# Revit family: Water_Heaters_HAJDU_HAJDU-HPT-200-and-200C_
name_source: partatom
category: Mechanical Equipment
units: mm (PartAtom-declared; Revit-internal decimal feet)

## family parameters
Always vertical = Yes
Classification = None
Cut with Voids When Loaded = No
Maintain Annotation Orientation = No
OmniClass Number = 23.31.29.13
OmniClass Title = Hot Water Tank Heaters
Part Type = Normal
Room Calculation Point = No
Round Connector Dimension = Use Diameter
Shared = No
Work Plane-Based = Yes

## types (2) — shared parameters
COP 20 °C = 3.36
COP 7 °C = 2.92
Case Material = Hajdu - Felület - Fehér
Cirkuláció bemenet = 19.05 mm  [stored 0.0625 ft]
Csapolási profil = L
Csatlakozás leírása = Elektromos csatlakozó
Default Elevation = 1219.2 mm  [stored 4 ft]
Description = A HB készülékek mellett, a HAJDU hőszivattyús forróvíztárolók másik termékcsaládja a HPT-k. Kisebb teljesítmény felvétel jellemzi max. hőszivattyús üzemmódban, illetve vízmelegítési hatékonysága is magasabb.A hőszivattyúból kiáramló levegővel hűthetjük a belső helyiségeket, vagy ha a lehűtött levegőt kivezetjük, akkor a helyiség vagy lakás szellőzését is szolgálhatja. A készülék a ház szellőztető rendszeréhez is csatlakoztatható. A használati melegvíz előállítás mellett így, ezek a készülékek a szellőztetésben, légkondicionálásban és páramentesítésben is szerepet kaphatnak.  Az elektromos fűtőtest segítségével a használati víz 65 °C-ra felmelegíthető.
Elektromos bekötés = fix
Energiahatékonysági osztály = A+
Feszültség = 230 V
Frekvencia = 50 Hz
Fázisok száma = 1
Hoszigetelés/vastagság = freonmentes PUR szigetelés / 50 mm
Hutoközeg/mennyiség = 1300g/R134a
Kompresszor teljesítmény felvétel max. = 900 W
Kompresszor teljesítmény felvétel átlagos = 515 W
Kondenzátor = biztonsági hőcserélő
Korrózióvédelem = speciális tűzzománc + Mg aktív anód
Látszólagos terhelés = 3680 VA
Légcsatorna csatlakozás = 160 mm  [stored 0.524934 ft]
Légáramlás = 125.0 L/s
Magasság = 1480 mm  [stored 4.85564 ft]
Manufacturer = HAJDU
Max. vízhomérséklet = 65 °C
Mg-anód karbantartás = anódfogyás kijelző
Muködési homérséklet tartomány = - 7– +38 °C
Mélység = 720 mm  [stored 2.3622 ft]
Névleges urtartalom = 200 l
Névleges üzemi nyomás = 0.6 MPa
Product Page URL = https://hajdurt.hu
Pótfuto teljesítmény = 1800 W
Rádiusz = 333.5 mm  [stored 1.09416 ft]
Rádiusz offset = 339.5 mm  [stored 1.11385 ft]
Teljesítménytényezo = 1
Típus = levegő (beltéri)
URL = https://hajdurt.hu
Védettségi fokozat = IPX4
Vízcsatlakozás = 19.05 mm  [stored 0.0625 ft]
Áramfelvétel = 16 A
Átméro = 667 mm  [stored 2.18832 ft]
Érintésvédelmi osztály = I.

## per-type parameters (varying)
| type | Hocserélo felulete | Hocserélo futoközeg belépés | Hocserélo futoközeg kilépés | Model | Tömeg |
| HPT 200C | 1.5 m2 | 19.05 mm  [stored 0.0625 ft] | 19.05 mm  [stored 0.0625 ft] | HAJDU HPT 200C | 116.00 kg |
| HPT 200 |  | 0 mm  [stored 0 ft] | 0 mm  [stored 0 ft] | HAJDU HPT 200 | 92.00 kg |

note: [stored X ft] marks values corroborated as IEEE doubles in the binary element streams (Revit-internal decimal feet)

## geometry (parser evidence)
native form markers: Sweep x4
no freeform markers — native parametric forms only
